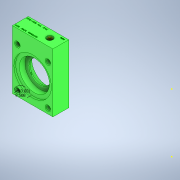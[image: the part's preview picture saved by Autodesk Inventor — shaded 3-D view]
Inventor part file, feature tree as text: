
AUTODESK INVENTOR PART (.ipt)
format: ipt  version: 2020 (Build 240168000, 168)  size: 539,648 bytes
history: native  units: in
note: dims shown in document units (in); Inventor stores cm internally (conversion verified against a paired STEP export)
features: sketch x5, hole x4, extrude x3, imported_body x1
ambient origin geometry x8: Origin, YZ Plane, XZ Plane, XY Plane, X Axis, Y Axis, Z Axis, Center Point
bodies: Solid1 (feature_tree)
feature tree (13):
  extrude  "Extrusion1"  Depth=0.3937in TaperAngle=0.0deg
  extrude  "Extrusion2"  Depth=0.3743in
  sketch  "Sketch3"  dims[d11=0.213in d12=0.2362in d13=0.4375in d14=0.25in d15=0.563in d16=0.375in d17=0.0in d18=0.3743in]
  hole  "Hole1"  [1 undecoded]
  hole  "Hole2"  [1 undecoded]
  sketch  "Sketch4"  dims[d19=0.0in]
  hole  "Hole3"  [1 undecoded]
  hole  "Hole4"  [1 undecoded]
  extrude  "Extrusion3"  [1 undecoded]
  sketch  "Sketch1"  dims[d0=0.6398in d1=0.0in d2=0.3937in d3=0.0in]
  sketch  "Sketch2"  dims[d4=0.03in d5=0.2362in d6=0.4375in d7=0.25in d8=0.563in d9=0.9843in d10=0.8108in]
  sketch  "Sketch5"  dims[d20=0.213in d21=0.2362in d22=0.4375in d23=0.25in d24=0.563in d25=0.375in d26=0.0in d27=0.03in d28=0.2362in d29=0.4375in d30=0.25in d31=0.563in d32=1.0in d33=0.8108in d34=0.1181in d35=0.0in]
  imported_body  "Base1"
note: 5 required parameter values undecoded (feature->parameter linkage not recoverable at this tier; creation-order binding heuristic only, values carry confidence <= 0.55)
